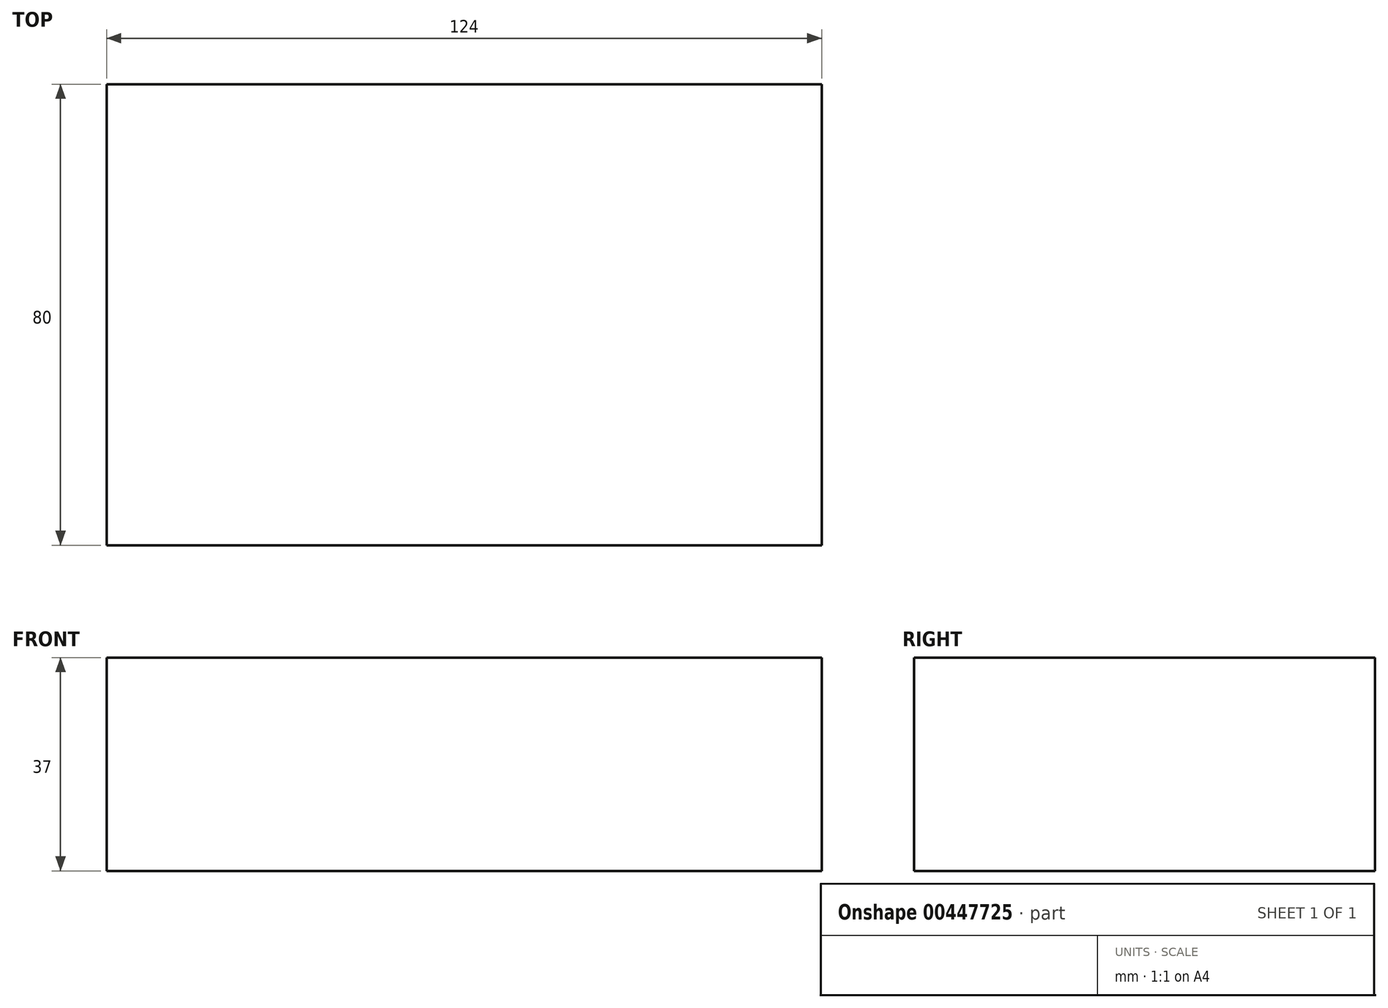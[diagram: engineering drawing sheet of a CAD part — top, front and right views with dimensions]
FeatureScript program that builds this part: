
annotation { "Feature Type Name" : "Feature", "Feature Type Description" : "" }
export const myFeature = defineFeature(function(context is Context, id is Id, definition is map)
    precondition{}
    {
        {
            var Q0;
            Q0=qCreatedBy(makeId("Top.planeOp"),FACE);
            var sketch = newSketch(context, id + "F0", { "sketchPlane" : qUnion([Q0])});
            skLineSegment(sketch, "E0.bottom", {"start": v(-62, 40) * mm, "end": v(62, 40) * mm});
            skLineSegment(sketch, "E0.top", {"start": v(-62, -40) * mm, "end": v(62, -40) * mm});
            skLineSegment(sketch, "E0.left", {"start": v(-62, 40) * mm, "end": v(-62, -40) * mm});
            skLineSegment(sketch, "E0.right", {"start": v(62, 40) * mm, "end": v(62, -40) * mm});
            skPoint(sketch, "E0.middle", {"position": v(0, 0) * mm});
            skSolve(sketch);
        }
        {
            var Q0;
            Q0=makeQuery(id+"F0.imprint","IMPRINT",FACE,{"disambiguationData":[TD([[makeQuery(id+"F0.imprint","IMPRINT",EDGE,{"derivedFrom":sQuery(id+"F0.wireOp",EDGE,"E0.bottom")}),-1.0]])]});
            extrude(context, id + "F1", {"entities" : qUnion([Q0]), "depth" : 37 * mm});
        }
    });
